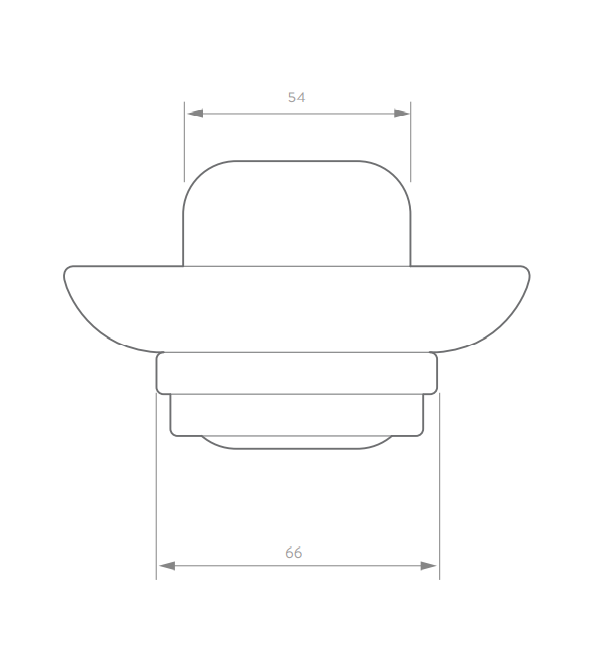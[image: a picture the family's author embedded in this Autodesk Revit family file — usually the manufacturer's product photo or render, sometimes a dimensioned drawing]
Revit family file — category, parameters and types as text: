
# Revit family: PM1055551_Jabonera Palma
name_source: partatom
category: Plumbing Fixtures
units: mm (PartAtom-declared; Revit-internal decimal feet)

## family parameters
Always vertical = Yes
Cut with Voids When Loaded = No
Host = Wall
OmniClass Number = 23.19.31.17.11
OmniClass Title = Bathroom Units
Part Type = Normal
Room Calculation Point = No
Round Connector Dimension = Use Diameter
Shared = No

## types (1)
- Jabonera Palma
    Alto = 68 mm
    Ancho = 66 mm  [stored 0.216535 ft]
    Creado por = BIMBAU
    Default Elevation = 0 mm  [stored 0 ft]
    Description = Accesorios que reflejan las últimas tendencias de diseño convirtiéndose así en el mejor complemento para su baño. Contando con un sistema de instalación oculto en material metálico cromado que facilitan su limpieza y mantienen el diseño estilizado.
    Fecha de creación = 04/05/2021
    Garantía = 3 años - 3 años Cromado.
    Manufacturer = Corona.
    Material = Corona_Cromado
    Material 2 = Corona_Plastico_Blanco
    Model = PM1055551_Jabonera Palma.
    Peso Neto aprox = 1090 gr. (2.4030 lb).
    Profundidad = 119 mm  [stored 0.39042 ft]
    Recubrimientos = Resistente a la corrosión, pelado y decoloración por agua. Recubrimientos no tóxicos. Producto para uso doméstico.

note: [stored X ft] marks values corroborated as IEEE doubles in the binary element streams (Revit-internal decimal feet)

## geometry (parser evidence)
native form markers: Sweep x7
no freeform markers — native parametric forms only
